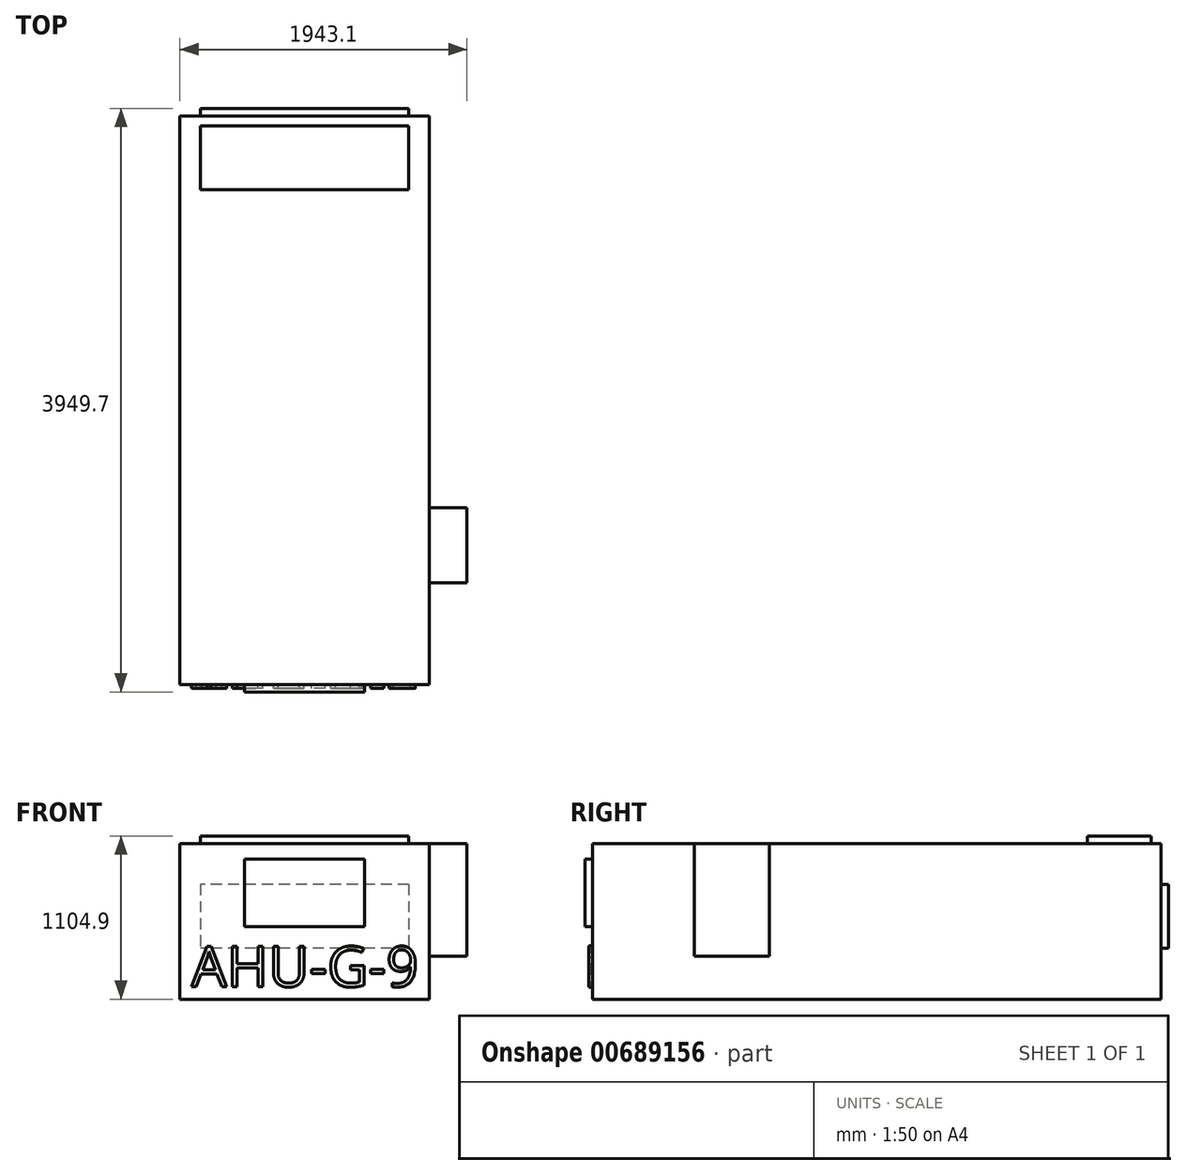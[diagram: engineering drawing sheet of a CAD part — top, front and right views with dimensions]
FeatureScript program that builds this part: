
annotation { "Feature Type Name" : "Feature", "Feature Type Description" : "" }
export const myFeature = defineFeature(function(context is Context, id is Id, definition is map)
    precondition{}
    {
        {
            var Q0;
            Q0=qCreatedBy(makeId("Front.planeOp"),FACE);
            var sketch = newSketch(context, id + "F0", { "sketchPlane" : qUnion([Q0])});
            skLineSegment(sketch, "E0.bottom", {"start": v(-639.94, 501.66) * mm, "end": v(1049.16, 501.66) * mm});
            skLineSegment(sketch, "E0.top", {"start": v(-639.94, -552.44) * mm, "end": v(1049.16, -552.44) * mm});
            skLineSegment(sketch, "E0.left", {"start": v(-639.94, 501.66) * mm, "end": v(-639.94, -552.44) * mm});
            skLineSegment(sketch, "E0.right", {"start": v(1049.16, 501.66) * mm, "end": v(1049.16, -552.44) * mm});
            skSolve(sketch);
        }
        {
            var Q0;
            Q0=qSketchRegion(id+"F0",true);
            extrude(context, id + "F1", {"entities" : qUnion([Q0]), "depth" : 3848.1 * mm, "offsetDistance" : 25.4 * mm});
        }
        {
            var Q0;
            Q0=makeQuery(id+"F1.opExtrude","CAP_FACE",FACE,{"disambiguationData":[OSD([sQuery(id+"F0.wireOp",EDGE,"E0.bottom"),sQuery(id+"F0.wireOp",EDGE,"E0.top"),sQuery(id+"F0.wireOp",EDGE,"E0.left"),sQuery(id+"F0.wireOp",EDGE,"E0.right")])],"isStart":false});
            var sketch = newSketch(context, id + "F2", { "sketchPlane" : qUnion([Q0])});
            skLineSegment(sketch, "E1.bottom", {"start": v(-201.8, 396.89) * mm, "end": v(611, 396.89) * mm});
            skLineSegment(sketch, "E1.top", {"start": v(-201.8, -60.31) * mm, "end": v(611, -60.31) * mm});
            skLineSegment(sketch, "E1.left", {"start": v(-201.8, 396.89) * mm, "end": v(-201.8, -60.31) * mm});
            skLineSegment(sketch, "E1.right", {"start": v(611, 396.89) * mm, "end": v(611, -60.31) * mm});
            skSolve(sketch);
        }
        {
            var Q0;
            Q0=makeQuery(id+"F2.imprint","IMPRINT",FACE,{"disambiguationData":[TD([[makeQuery(id+"F2.imprint","IMPRINT",EDGE,{"derivedFrom":sQuery(id+"F2.wireOp",EDGE,"E1.bottom")}),-1.0]])]});
            extrude(context, id + "F3", {"entities" : qUnion([Q0]), "operationType" : NewBodyOperationType.ADD, "depth" : 50.8 * mm, "offsetDistance" : 25.4 * mm});
        }
        {
            var Q0;
            Q0=makeQuery(id+"F1.opExtrude","SWEPT_FACE",FACE,{"disambiguationData":[OSD([sQuery(id+"F0.wireOp",EDGE,"E0.right")])]});
            var sketch = newSketch(context, id + "F4", { "sketchPlane" : qUnion([Q0])});
            skLineSegment(sketch, "E2.bottom", {"start": v(-3159.13, 501.66) * mm, "end": v(-2651.13, 501.66) * mm});
            skLineSegment(sketch, "E2.top", {"start": v(-3159.13, -260.34) * mm, "end": v(-2651.13, -260.34) * mm});
            skLineSegment(sketch, "E2.left", {"start": v(-3159.13, 501.66) * mm, "end": v(-3159.13, -260.34) * mm});
            skLineSegment(sketch, "E2.right", {"start": v(-2651.13, 501.66) * mm, "end": v(-2651.13, -260.34) * mm});
            skSolve(sketch);
        }
        {
            var Q0;
            Q0 = qSketchRegion(id + "F4", true);
            extrude(context, id + "F5", {"entities" : qUnion([Q0]), "depth" : 254 * mm, "offsetDistance" : 25.4 * mm});
        }
        {
            var Q0;
            Q0=makeQuery(id+"F1.opExtrude","CAP_FACE",FACE,{"disambiguationData":[OSD([sQuery(id+"F0.wireOp",EDGE,"E0.bottom"),sQuery(id+"F0.wireOp",EDGE,"E0.top"),sQuery(id+"F0.wireOp",EDGE,"E0.left"),sQuery(id+"F0.wireOp",EDGE,"E0.right")])],"isStart":false});
            var sketch = newSketch(context, id + "F6", { "sketchPlane" : qUnion([Q0])});
            skText(sketch, "E3", { "text": "AHU-G-9", "fontName": "OpenSans-Regular.ttf"});
            const initialGuessF6  = {"E3": [-0.56358, -0.46768, 1, 0, 0.27381]};
            skSetInitialGuess(sketch, initialGuessF6);
            skSolve(sketch);
        }
        {
            var Q0;
            Q0 = qSketchRegion(id + "F6", true);
            extrude(context, id + "F7", {"entities" : qUnion([Q0]), "operationType" : NewBodyOperationType.ADD, "depth" : 25.4 * mm, "offsetDistance" : 25.4 * mm});
        }
        {
            var Q0;
            Q0=makeQuery(id+"F1.opExtrude","CAP_FACE",FACE,{"disambiguationData":[OSD([sQuery(id+"F0.wireOp",EDGE,"E0.bottom"),sQuery(id+"F0.wireOp",EDGE,"E0.top"),sQuery(id+"F0.wireOp",EDGE,"E0.left"),sQuery(id+"F0.wireOp",EDGE,"E0.right")])],"isStart":true});
            var sketch = newSketch(context, id + "F8", { "sketchPlane" : qUnion([Q0])});
            skLineSegment(sketch, "E4.bottom", {"start": v(-909.46, 225.44) * mm, "end": v(500.24, 225.44) * mm});
            skLineSegment(sketch, "E4.top", {"start": v(-909.46, -206.36) * mm, "end": v(500.24, -206.36) * mm});
            skLineSegment(sketch, "E4.left", {"start": v(-909.46, 225.44) * mm, "end": v(-909.46, -206.36) * mm});
            skLineSegment(sketch, "E4.right", {"start": v(500.24, 225.44) * mm, "end": v(500.24, -206.36) * mm});
            skSolve(sketch);
        }
        {
            var Q0;
            Q0 = qSketchRegion(id + "F8", true);
            extrude(context, id + "F9", {"entities" : qUnion([Q0]), "operationType" : NewBodyOperationType.ADD, "depth" : 50.8 * mm, "offsetDistance" : 25.4 * mm});
        }
        {
            var Q0;
            Q0=makeQuery(id+"F1.opExtrude","SWEPT_FACE",FACE,{"disambiguationData":[OSD([sQuery(id+"F0.wireOp",EDGE,"E0.bottom")])]});
            var sketch = newSketch(context, id + "F10", { "sketchPlane" : qUnion([Q0])});
            skLineSegment(sketch, "E5.bottom", {"start": v(-500.24, -66.68) * mm, "end": v(909.46, -66.68) * mm});
            skLineSegment(sketch, "E5.top", {"start": v(-500.24, -498.48) * mm, "end": v(909.46, -498.48) * mm});
            skLineSegment(sketch, "E5.left", {"start": v(-500.24, -66.68) * mm, "end": v(-500.24, -498.48) * mm});
            skLineSegment(sketch, "E5.right", {"start": v(909.46, -66.67) * mm, "end": v(909.46, -498.47) * mm});
            skSolve(sketch);
        }
        {
            var Q0;
            Q0 = qSketchRegion(id + "F10", true);
            extrude(context, id + "F11", {"entities" : qUnion([Q0]), "operationType" : NewBodyOperationType.ADD, "depth" : 50.8 * mm, "offsetDistance" : 25.4 * mm});
        }
    });
